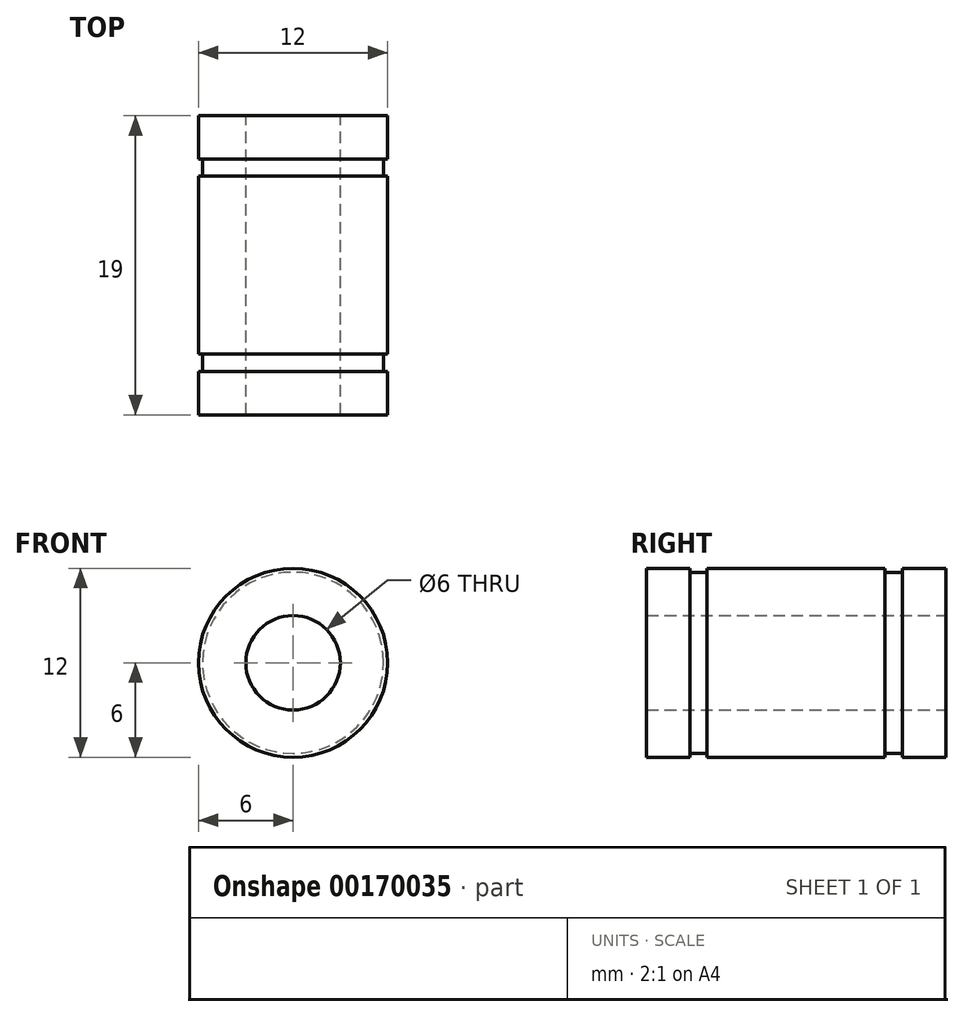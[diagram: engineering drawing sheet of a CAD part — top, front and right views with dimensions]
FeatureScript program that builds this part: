
annotation { "Feature Type Name" : "Feature", "Feature Type Description" : "" }
export const myFeature = defineFeature(function(context is Context, id is Id, definition is map)
    precondition{}
    {
        {
            var Q0;
            Q0=qCreatedBy(makeId("Front.planeOp"),FACE);
            var sketch = newSketch(context, id + "F0", { "sketchPlane" : qUnion([Q0])});
            skCircle(sketch, "E0", {"center": v(0, 0) * mm, "radius": 6 * mm});
            skCircle(sketch, "E1", {"center": v(0, 0) * mm, "radius": 3 * mm});
            skSolve(sketch);
        }
        {
            var Q0;
            Q0=qSketchRegion(id+"F0",true);
            extrude(context, id + "F1", {"entities" : qUnion([Q0]), "depth" : 2.75 * mm});
        }
        {
            var Q0;
            Q0=makeQuery(id+"F1.opExtrude","CAP_FACE",FACE,{"disambiguationData":[OSD([sQuery(id+"F0.wireOp",EDGE,"E0"),sQuery(id+"F0.wireOp",EDGE,"E1")])],"isStart":false});
            var sketch = newSketch(context, id + "F2", { "sketchPlane" : qUnion([Q0])});
            skCircle(sketch, "E2", {"center": v(0, 0) * mm, "radius": 5.75 * mm});
            skSolve(sketch);
        }
        {
            var Q0;
            Q0=makeQuery(id+"F2.imprint","IMPRINT",FACE,{"disambiguationData":[TD([[makeQuery(id+"F2.imprint","IMPRINT",EDGE,{"derivedFrom":sQuery(id+"F2.wireOp",EDGE,"E2")}),1.0]])]});
            extrude(context, id + "F3", {"entities" : qUnion([Q0]), "operationType" : NewBodyOperationType.ADD, "depth" : 1.1 * mm});
        }
        {
            var Q0;
            Q0=makeQuery(id+"F3.opExtrude","CAP_FACE",FACE,{"disambiguationData":[OSD([sQuery(id+"F0.wireOp",EDGE,"E1"),sQuery(id+"F2.wireOp",EDGE,"E2")])],"isStart":false});
            var sketch = newSketch(context, id + "F4", { "sketchPlane" : qUnion([Q0])});
            skCircle(sketch, "E3.0", {"center": v(0, 0) * mm, "radius": 6 * mm});
            skSolve(sketch);
        }
        {
            var Q0;
            Q0=makeQuery(id+"F4.imprint","IMPRINT",FACE,{"disambiguationData":[TD([[makeQuery(id+"F4.imprint","IMPRINT",EDGE,{"derivedFrom":makeQuery(id+"F3.opExtrude","CAP_EDGE",EDGE,{"disambiguationData":[OSD([sQuery(id+"F2.wireOp",EDGE,"E2")])],"isStart":false})}),1.0]])]});
            var Q1;
            Q1=makeQuery(id+"F4.imprint","IMPRINT",FACE,{"disambiguationData":[TD([[makeQuery(id+"F4.imprint","IMPRINT",EDGE,{"derivedFrom":sQuery(id+"F4.wireOp",EDGE,"E3.0")}),1.0]])]});
            extrude(context, id + "F5", {"entities" : qUnion([Q0, Q1]), "operationType" : NewBodyOperationType.ADD, "depth" : 11.3 * mm});
        }
        {
            var Q0;
            Q0=makeQuery(id+"F5.opExtrude","CAP_FACE",FACE,{"disambiguationData":[OSD([sQuery(id+"F0.wireOp",EDGE,"E1"),sQuery(id+"F4.wireOp",EDGE,"E3.0")])],"isStart":false});
            var sketch = newSketch(context, id + "F6", { "sketchPlane" : qUnion([Q0])});
            skCircle(sketch, "E4.0", {"center": v(0, 0) * mm, "radius": 5.75 * mm});
            skSolve(sketch);
        }
        {
            var Q0;
            Q0=makeQuery(id+"F6.imprint","IMPRINT",FACE,{"disambiguationData":[TD([[makeQuery(id+"F6.imprint","IMPRINT",EDGE,{"derivedFrom":sQuery(id+"F6.wireOp",EDGE,"E4.0")}),1.0]])]});
            extrude(context, id + "F7", {"entities" : qUnion([Q0]), "operationType" : NewBodyOperationType.ADD, "depth" : 1.1 * mm});
        }
        {
            var Q0;
            Q0=makeQuery(id+"F7.opExtrude","CAP_FACE",FACE,{"disambiguationData":[OSD([sQuery(id+"F0.wireOp",EDGE,"E1"),sQuery(id+"F6.wireOp",EDGE,"E4.0")])],"isStart":false});
            var sketch = newSketch(context, id + "F8", { "sketchPlane" : qUnion([Q0])});
            skCircle(sketch, "E5.0", {"center": v(0, 0) * mm, "radius": 6 * mm});
            skSolve(sketch);
        }
        {
            var Q0;
            Q0=makeQuery(id+"F8.imprint","IMPRINT",FACE,{"disambiguationData":[TD([[makeQuery(id+"F8.imprint","IMPRINT",EDGE,{"derivedFrom":sQuery(id+"F8.wireOp",EDGE,"E5.0")}),1.0]])]});
            var Q1;
            Q1=makeQuery(id+"F8.imprint","IMPRINT",FACE,{"disambiguationData":[TD([[makeQuery(id+"F8.imprint","IMPRINT",EDGE,{"derivedFrom":makeQuery(id+"F7.opExtrude","CAP_EDGE",EDGE,{"disambiguationData":[OSD([sQuery(id+"F6.wireOp",EDGE,"E4.0")])],"isStart":false})}),1.0]])]});
            extrude(context, id + "F9", {"entities" : qUnion([Q0, Q1]), "operationType" : NewBodyOperationType.ADD, "depth" : 2.75 * mm, "offsetDistance" : 25 * mm});
        }
    });
